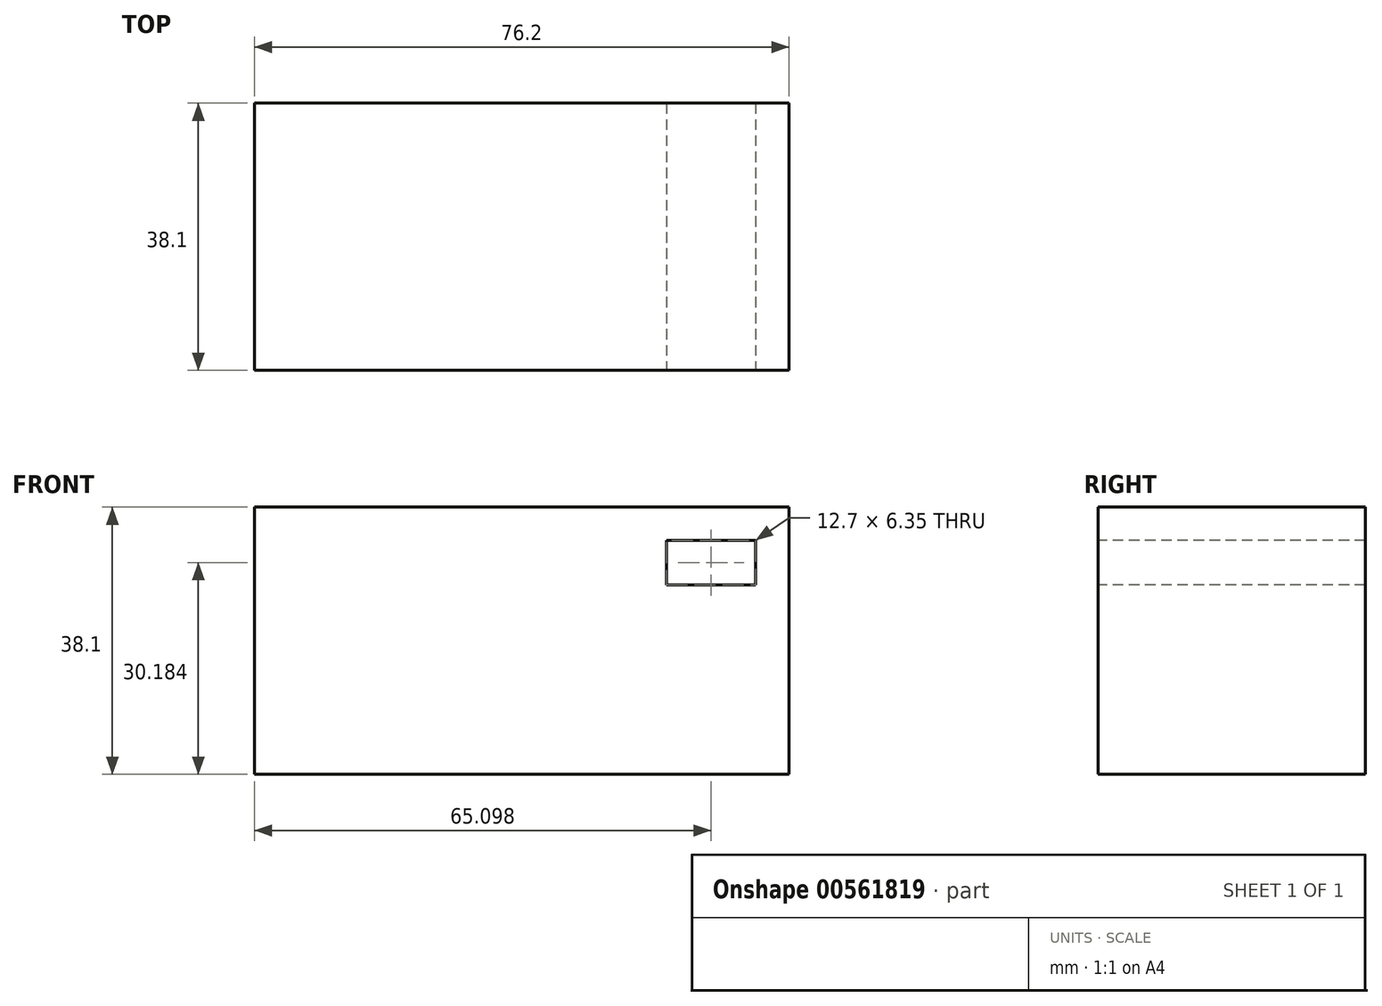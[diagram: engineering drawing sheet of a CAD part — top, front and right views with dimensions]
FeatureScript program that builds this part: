
annotation { "Feature Type Name" : "Feature", "Feature Type Description" : "" }
export const myFeature = defineFeature(function(context is Context, id is Id, definition is map)
    precondition{}
    {
        {
            var Q0;
            Q0=qCreatedBy(makeId("Front.planeOp"),FACE);
            var sketch = newSketch(context, id + "F0", { "sketchPlane" : qUnion([Q0])});
            skLineSegment(sketch, "E0.bottom", {"start": v(-38.1, 19.05) * mm, "end": v(38.1, 19.05) * mm});
            skLineSegment(sketch, "E0.top", {"start": v(-38.1, -19.05) * mm, "end": v(38.1, -19.05) * mm});
            skLineSegment(sketch, "E0.left", {"start": v(-38.1, 19.05) * mm, "end": v(-38.1, -19.05) * mm});
            skLineSegment(sketch, "E0.right", {"start": v(38.1, 19.05) * mm, "end": v(38.1, -19.05) * mm});
            skPoint(sketch, "E0.middle", {"position": v(0, 0) * mm});
            skSolve(sketch);
        }
        {
            var Q0;
            Q0=makeQuery(id+"F0.imprint","IMPRINT",FACE,{"disambiguationData":[TD([[makeQuery(id+"F0.imprint","IMPRINT",EDGE,{"derivedFrom":sQuery(id+"F0.wireOp",EDGE,"E0.bottom")}),-1.0]])]});
            extrude(context, id + "F1", {"entities" : qUnion([Q0]), "depth" : 38.1 * mm, "offsetDistance" : 25.4 * mm});
        }
        {
            var Q0;
            Q0=makeQuery(id+"F1.opExtrude","CAP_FACE",FACE,{"disambiguationData":[OSD([sQuery(id+"F0.wireOp",EDGE,"E0.bottom"),sQuery(id+"F0.wireOp",EDGE,"E0.top"),sQuery(id+"F0.wireOp",EDGE,"E0.left"),sQuery(id+"F0.wireOp",EDGE,"E0.right")])],"isStart":false});
            var sketch = newSketch(context, id + "F2", { "sketchPlane" : qUnion([Q0])});
            skLineSegment(sketch, "E1.bottom", {"start": v(33.35, 14.3) * mm, "end": v(20.65, 14.3) * mm});
            skLineSegment(sketch, "E1.top", {"start": v(33.35, 7.96) * mm, "end": v(20.65, 7.96) * mm});
            skLineSegment(sketch, "E1.left", {"start": v(33.35, 14.3) * mm, "end": v(33.35, 7.96) * mm});
            skLineSegment(sketch, "E1.right", {"start": v(20.65, 14.3) * mm, "end": v(20.65, 7.96) * mm});
            skSolve(sketch);
        }
        {
            var Q0;
            Q0 = qSketchRegion(id + "F2", true);
            extrude(context, id + "F3", {"entities" : qUnion([Q0]), "operationType" : NewBodyOperationType.REMOVE, "oppositeDirection" : true, "depth" : 38.1 * mm, "offsetDistance" : 25.4 * mm});
        }
    });
